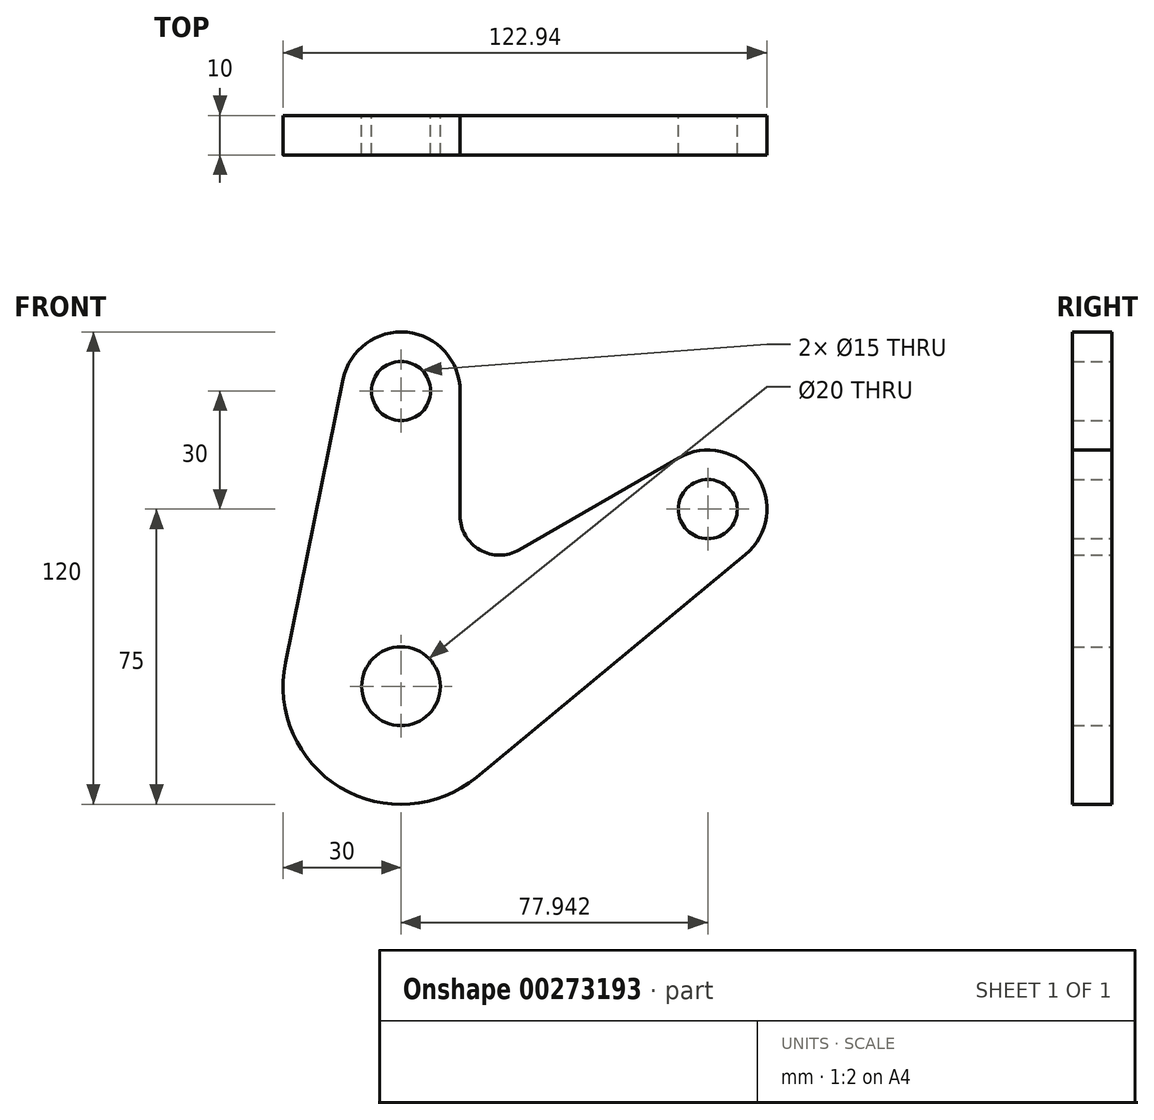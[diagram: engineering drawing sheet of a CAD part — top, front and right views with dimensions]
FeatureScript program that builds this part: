
annotation { "Feature Type Name" : "Feature", "Feature Type Description" : "" }
export const myFeature = defineFeature(function(context is Context, id is Id, definition is map)
    precondition{}
    {
        {
            var Q0;
            Q0=qCreatedBy(makeId("Front.planeOp"),FACE);
            var sketch = newSketch(context, id + "F0", { "sketchPlane" : qUnion([Q0])});
            skLineSegment(sketch, "E0", {"start": v(0, 0) * mm, "end": v(77.94, 45) * mm, "construction": true});
            skLineSegment(sketch, "E1", {"start": v(0, 0) * mm, "end": v(0, 75) * mm, "construction": true});
            skCircle(sketch, "E2", {"center": v(0, 0) * mm, "radius": 10 * mm});
            skCircle(sketch, "E3", {"center": v(0, 75) * mm, "radius": 7.5 * mm});
            skCircle(sketch, "E4", {"center": v(77.94, 45) * mm, "radius": 7.5 * mm});
            skLineSegment(sketch, "E5", {"start": v(-14.7, 78) * mm, "end": v(-29.4, 6) * mm});
            skLineSegment(sketch, "E6", {"start": v(19.12, -23.12) * mm, "end": v(87.5, 33.44) * mm});
            skLineSegment(sketch, "E7", {"start": v(70.44, 58) * mm, "end": v(30, 34.64) * mm});
            skLineSegment(sketch, "E8", {"start": v(15, 43.3) * mm, "end": v(15, 75) * mm});
            skArc(sketch, "E9", {"start": v(15, 43.3) * mm, "mid": v(20, 34.64) * mm, "end": v(30, 34.64) * mm});
            skArc(sketch, "E10", {"start": v(15, 75) * mm, "mid": v(1.5, 89.92) * mm, "end": v(-14.7, 78) * mm});
            skArc(sketch, "E11", {"start": v(-29.4, 6) * mm, "mid": v(-15.44, -25.72) * mm, "end": v(19.12, -23.12) * mm});
            skArc(sketch, "E12", {"start": v(87.5, 33.44) * mm, "mid": v(90.26, 53.56) * mm, "end": v(70.44, 58) * mm});
            skSolve(sketch);
        }
        {
            var Q0;
            Q0=makeQuery(id+"F0.imprint","IMPRINT",FACE,{"disambiguationData":[TD([[makeQuery(id+"F0.imprint","IMPRINT",EDGE,{"derivedFrom":sQuery(id+"F0.wireOp",EDGE,"E2")}),-1.0]])]});
            extrude(context, id + "F1", {"entities" : qUnion([Q0]), "depth" : 10 * mm});
        }
    });
